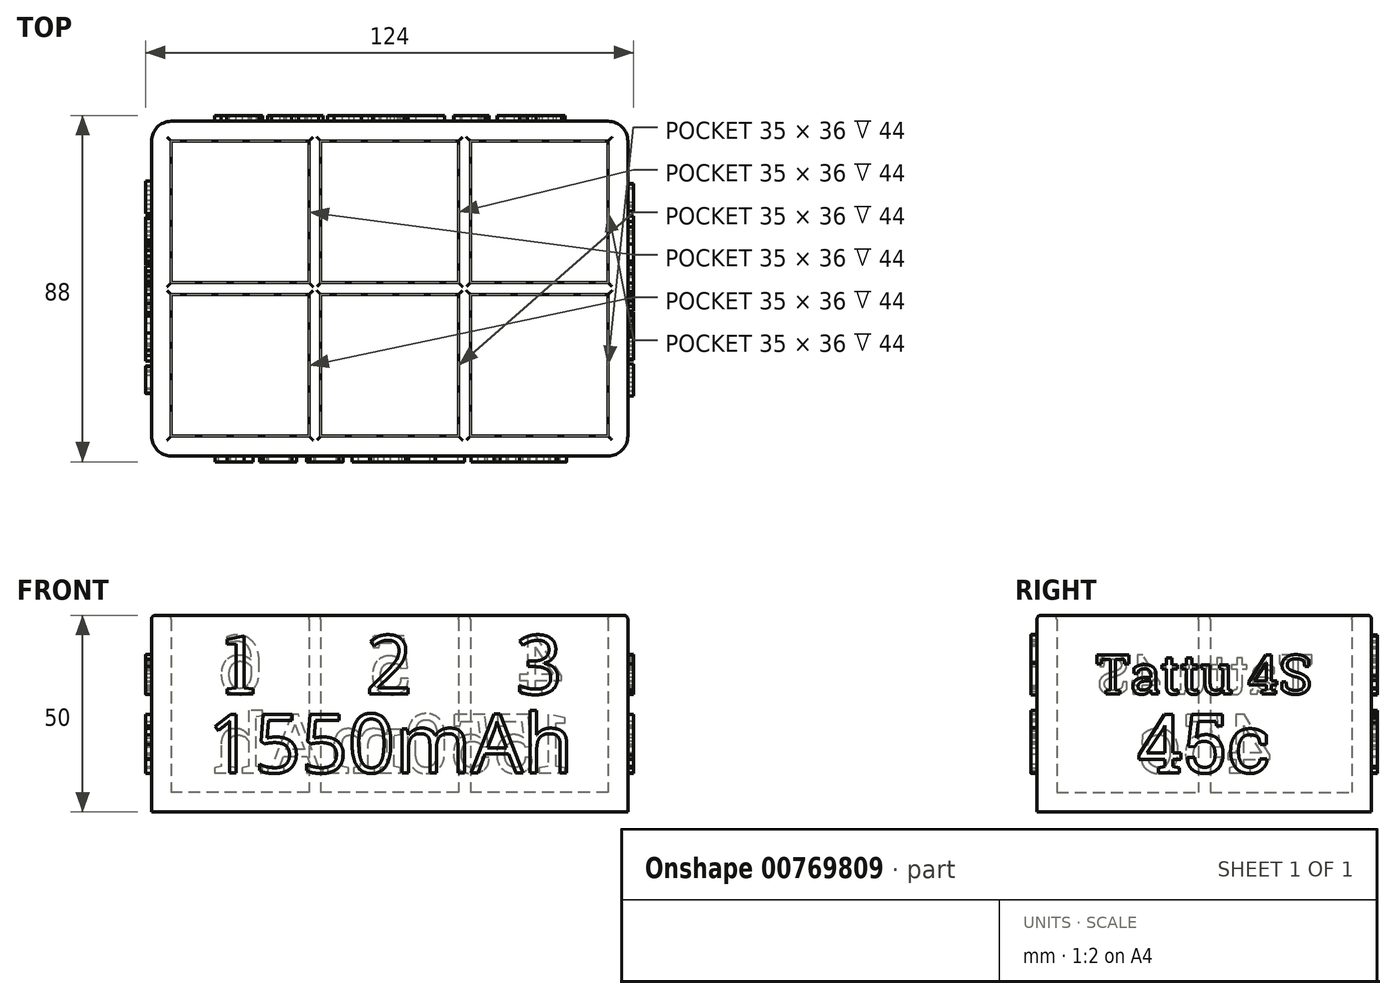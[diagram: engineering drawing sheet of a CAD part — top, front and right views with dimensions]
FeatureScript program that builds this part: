
annotation { "Feature Type Name" : "Feature", "Feature Type Description" : "" }
export const myFeature = defineFeature(function(context is Context, id is Id, definition is map)
    precondition{}
    {
        {
            var Q0;
            Q0=qCreatedBy(makeId("Top.planeOp"),FACE);
            var sketch = newSketch(context, id + "F0", { "sketchPlane" : qUnion([Q0])});
            skLineSegment(sketch, "E0.bottom", {"start": v(17.5, -18) * mm, "end": v(-17.5, -18) * mm});
            skLineSegment(sketch, "E0.top", {"start": v(17.5, 18) * mm, "end": v(-17.5, 18) * mm});
            skLineSegment(sketch, "E0.left", {"start": v(17.5, -18) * mm, "end": v(17.5, 18) * mm});
            skLineSegment(sketch, "E0.right", {"start": v(-17.5, -18) * mm, "end": v(-17.5, 18) * mm});
            skPoint(sketch, "E0.middle", {"position": v(0, 0) * mm});
            skLineSegment(sketch, "E1.0.1.0", {"start": v(17.5, 57) * mm, "end": v(-17.5, 57) * mm});
            skLineSegment(sketch, "E1.0.1.1", {"start": v(-17.5, 21) * mm, "end": v(-17.5, 57) * mm});
            skLineSegment(sketch, "E1.0.1.2", {"start": v(17.5, 21) * mm, "end": v(-17.5, 21) * mm});
            skLineSegment(sketch, "E1.0.1.3", {"start": v(17.5, 21) * mm, "end": v(17.5, 57) * mm});
            skLineSegment(sketch, "E1.1.0.0", {"start": v(55.5, 18) * mm, "end": v(20.5, 18) * mm});
            skLineSegment(sketch, "E1.1.0.1", {"start": v(20.5, -18) * mm, "end": v(20.5, 18) * mm});
            skLineSegment(sketch, "E1.1.0.2", {"start": v(55.5, -18) * mm, "end": v(20.5, -18) * mm});
            skLineSegment(sketch, "E1.1.0.3", {"start": v(55.5, -18) * mm, "end": v(55.5, 18) * mm});
            skLineSegment(sketch, "E1.1.1.0", {"start": v(55.5, 57) * mm, "end": v(20.5, 57) * mm});
            skLineSegment(sketch, "E1.1.1.1", {"start": v(20.5, 21) * mm, "end": v(20.5, 57) * mm});
            skLineSegment(sketch, "E1.1.1.2", {"start": v(55.5, 21) * mm, "end": v(20.5, 21) * mm});
            skLineSegment(sketch, "E1.1.1.3", {"start": v(55.5, 21) * mm, "end": v(55.5, 57) * mm});
            skLineSegment(sketch, "E1.2.0.0", {"start": v(93.5, 18) * mm, "end": v(58.5, 18) * mm});
            skLineSegment(sketch, "E1.2.0.1", {"start": v(58.5, -18) * mm, "end": v(58.5, 18) * mm});
            skLineSegment(sketch, "E1.2.0.2", {"start": v(93.5, -18) * mm, "end": v(58.5, -18) * mm});
            skLineSegment(sketch, "E1.2.0.3", {"start": v(93.5, -18) * mm, "end": v(93.5, 18) * mm});
            skLineSegment(sketch, "E1.2.1.0", {"start": v(93.5, 57) * mm, "end": v(58.5, 57) * mm});
            skLineSegment(sketch, "E1.2.1.1", {"start": v(58.5, 21) * mm, "end": v(58.5, 57) * mm});
            skLineSegment(sketch, "E1.2.1.2", {"start": v(93.5, 21) * mm, "end": v(58.5, 21) * mm});
            skLineSegment(sketch, "E1.2.1.3", {"start": v(93.5, 21) * mm, "end": v(93.5, 57) * mm});
            skLineSegment(sketch, "E1.direction1", {"start": v(-17.5, 18) * mm, "end": v(20.5, 18) * mm, "construction": true});
            skLineSegment(sketch, "E1.direction2", {"start": v(-17.5, 18) * mm, "end": v(-17.5, 57) * mm, "construction": true});
            skLineSegment(sketch, "E2.bottom", {"start": v(-22.5, 62) * mm, "end": v(98.5, 62) * mm});
            skLineSegment(sketch, "E2.top", {"start": v(-22.5, -23) * mm, "end": v(98.5, -23) * mm});
            skLineSegment(sketch, "E2.left", {"start": v(-22.5, 62) * mm, "end": v(-22.5, -23) * mm});
            skLineSegment(sketch, "E2.right", {"start": v(98.5, 62) * mm, "end": v(98.5, -23) * mm});
            skSolve(sketch);
        }
        {
            var Q0;
            Q0=makeQuery(id+"F0.imprint","IMPRINT",FACE,{"disambiguationData":[TD([[makeQuery(id+"F0.imprint","IMPRINT",EDGE,{"derivedFrom":sQuery(id+"F0.wireOp",EDGE,"E0.bottom")}),1.0]])]});
            var Q1;
            Q1=makeQuery(id+"F0.imprint","IMPRINT",FACE,{"disambiguationData":[TD([[makeQuery(id+"F0.imprint","IMPRINT",EDGE,{"derivedFrom":sQuery(id+"F0.wireOp",EDGE,"E0.bottom")}),-1.0]])]});
            var Q2;
            Q2=makeQuery(id+"F0.imprint","IMPRINT",FACE,{"disambiguationData":[TD([[makeQuery(id+"F0.imprint","IMPRINT",EDGE,{"derivedFrom":sQuery(id+"F0.wireOp",EDGE,"E1.0.1.0")}),1.0]])]});
            var Q3;
            Q3=makeQuery(id+"F0.imprint","IMPRINT",FACE,{"disambiguationData":[TD([[makeQuery(id+"F0.imprint","IMPRINT",EDGE,{"derivedFrom":sQuery(id+"F0.wireOp",EDGE,"E1.1.0.0")}),1.0]])]});
            var Q4;
            Q4=makeQuery(id+"F0.imprint","IMPRINT",FACE,{"disambiguationData":[TD([[makeQuery(id+"F0.imprint","IMPRINT",EDGE,{"derivedFrom":sQuery(id+"F0.wireOp",EDGE,"E1.1.1.0")}),1.0]])]});
            var Q5;
            Q5=makeQuery(id+"F0.imprint","IMPRINT",FACE,{"disambiguationData":[TD([[makeQuery(id+"F0.imprint","IMPRINT",EDGE,{"derivedFrom":sQuery(id+"F0.wireOp",EDGE,"E1.2.1.0")}),1.0]])]});
            var Q6;
            Q6=makeQuery(id+"F0.imprint","IMPRINT",FACE,{"disambiguationData":[TD([[makeQuery(id+"F0.imprint","IMPRINT",EDGE,{"derivedFrom":sQuery(id+"F0.wireOp",EDGE,"E1.2.0.0")}),1.0]])]});
            extrude(context, id + "F1", {"entities" : qUnion([Q0, Q1, Q2, Q3, Q4, Q5, Q6]), "oppositeDirection" : true, "depth" : 5 * mm, "offsetDistance" : 25 * mm});
        }
        {
            var Q0;
            Q0=makeQuery(id+"F0.imprint","IMPRINT",FACE,{"disambiguationData":[TD([[makeQuery(id+"F0.imprint","IMPRINT",EDGE,{"derivedFrom":sQuery(id+"F0.wireOp",EDGE,"E0.bottom")}),1.0]])]});
            extrude(context, id + "F2", {"entities" : qUnion([Q0]), "operationType" : NewBodyOperationType.ADD, "depth" : 45 * mm, "offsetDistance" : 25 * mm});
        }
        {
            var Q0;
            {var subQ0=sQuery(id+"F0.wireOp",EDGE,"E2.top");Q0=makeQuery(id+"F2.boolean.opBoolean","MERGE",FACE,{"derivedFrom":[makeQuery(id+"F1.opExtrude","SWEPT_FACE",FACE,{"disambiguationData":[OSD([subQ0])]}),makeQuery(id+"F2.opExtrude","SWEPT_FACE",FACE,{"disambiguationData":[OSD([subQ0])]})]});}
            var sketch = newSketch(context, id + "F3", { "sketchPlane" : qUnion([Q0])});
            skLineSegment(sketch, "E3", {"start": v(-59.84, 40) * mm, "end": v(123.55, 40) * mm, "construction": true});
            skLineSegment(sketch, "E4", {"start": v(-60.92, 25) * mm, "end": v(136.92, 25) * mm, "construction": true});
            skLineSegment(sketch, "E5", {"start": v(0, 84.5) * mm, "end": v(0, -27.53) * mm, "construction": true});
            skLineSegment(sketch, "E6", {"start": v(38, 84.3) * mm, "end": v(38, -24.79) * mm, "construction": true});
            skLineSegment(sketch, "E7", {"start": v(76, 82.1) * mm, "end": v(76, -27.2) * mm, "construction": true});
            skText(sketch, "E8", { "text": "1", "fontName": "RobotoSlab-Regular.ttf"});
            skText(sketch, "E9", { "text": "2", "fontName": "OpenSans-Regular.ttf"});
            skText(sketch, "E10", { "text": "3", "fontName": "OpenSans-Regular.ttf"});
            skText(sketch, "E11", { "text": "1550mAh", "fontName": "OpenSans-Regular.ttf"});
            const initialGuessF3  = {"E8": [-0.00455, 0.025, 1, 0, 0.015], "E9": [0.03193, 0.025, 1, 0, 0.015], "E10": [0.06998, 0.025, 1, 0, 0.015], "E11": [-0.00833, 0.005, 1, 0, 0.015]};
            skSetInitialGuess(sketch, initialGuessF3);
            skSolve(sketch);
        }
        {
            var Q0;
            {var subQ0=sQuery(id+"F0.wireOp",EDGE,"E2.bottom");Q0=makeQuery(id+"F2.boolean.opBoolean","MERGE",FACE,{"derivedFrom":[makeQuery(id+"F1.opExtrude","SWEPT_FACE",FACE,{"disambiguationData":[OSD([subQ0])]}),makeQuery(id+"F2.opExtrude","SWEPT_FACE",FACE,{"disambiguationData":[OSD([subQ0])]})]});}
            var sketch = newSketch(context, id + "F4", { "sketchPlane" : qUnion([Q0])});
            skLineSegment(sketch, "E12", {"start": v(-177.3, 40) * mm, "end": v(6.09, 40) * mm, "construction": true});
            skLineSegment(sketch, "E13", {"start": v(-178.38, 25) * mm, "end": v(19.46, 25) * mm, "construction": true});
            skLineSegment(sketch, "E14", {"start": v(-76, 83.96) * mm, "end": v(-76, -28.07) * mm, "construction": true});
            skLineSegment(sketch, "E15", {"start": v(-38, 83.76) * mm, "end": v(-38, -25.32) * mm, "construction": true});
            skLineSegment(sketch, "E16", {"start": v(0, 81.57) * mm, "end": v(0, -27.73) * mm, "construction": true});
            skText(sketch, "E17", { "text": "4", "fontName": "RobotoSlab-Regular.ttf"});
            skText(sketch, "E18", { "text": "5", "fontName": "RobotoSlab-Regular.ttf"});
            skText(sketch, "E19", { "text": "6", "fontName": "RobotoSlab-Regular.ttf"});
            skText(sketch, "E20", { "text": "1550mAh", "fontName": "RobotoSlab-Regular.ttf"});
            const initialGuessF4  = {"E17": [-0.08231, 0.025, 1, 0, 0.015], "E18": [-0.04364, 0.025, 1, 0, 0.015], "E19": [-0.00607, 0.025, 1, 0, 0.015], "E20": [-0.0838, 0.005, 1, 0, 0.015]};
            skSetInitialGuess(sketch, initialGuessF4);
            skSolve(sketch);
        }
        {
            var Q0;
            Q0 = qSketchRegion(id + "F4", true);
            extrude(context, id + "F5", {"entities" : qUnion([Q0]), "operationType" : NewBodyOperationType.ADD, "depth" : 1.5 * mm, "offsetDistance" : 25 * mm});
        }
        {
            var Q0;
            Q0 = qSketchRegion(id + "F3", true);
            extrude(context, id + "F6", {"entities" : qUnion([Q0]), "operationType" : NewBodyOperationType.ADD, "depth" : 1.5 * mm, "offsetDistance" : 25 * mm});
        }
        {
            var Q0;
            {var subQ0=sQuery(id+"F0.wireOp",EDGE,"E2.left");Q0=makeQuery(id+"F2.boolean.opBoolean","MERGE",FACE,{"derivedFrom":[makeQuery(id+"F1.opExtrude","SWEPT_FACE",FACE,{"disambiguationData":[OSD([subQ0])]}),makeQuery(id+"F2.opExtrude","SWEPT_FACE",FACE,{"disambiguationData":[OSD([subQ0])]})]});}
            var sketch = newSketch(context, id + "F7", { "sketchPlane" : qUnion([Q0])});
            skText(sketch, "E21", { "text": "Tattu 4S", "fontName": "RobotoSlab-Regular.ttf"});
            skLineSegment(sketch, "E22", {"start": v(-19.5, 84.5) * mm, "end": v(-19.5, -25.36) * mm, "construction": true});
            skLineSegment(sketch, "E23", {"start": v(49.66, 35) * mm, "end": v(-83.48, 35) * mm, "construction": true});
            skLineSegment(sketch, "E24", {"start": v(-87.5, 25) * mm, "end": v(51.92, 25) * mm, "construction": true});
            skText(sketch, "E25", { "text": "45c", "fontName": "RobotoSlab-Regular.ttf"});
            const initialGuessF7  = {"E21": [-0.04707, 0.025, 1, 0, 0.01], "E25": [-0.0368, 0.005, 1, 0, 0.015]};
            skSetInitialGuess(sketch, initialGuessF7);
            skSolve(sketch);
        }
        {
            var Q0;
            {var subQ0=sQuery(id+"F0.wireOp",EDGE,"E2.right");Q0=makeQuery(id+"F2.boolean.opBoolean","MERGE",FACE,{"derivedFrom":[makeQuery(id+"F1.opExtrude","SWEPT_FACE",FACE,{"disambiguationData":[OSD([subQ0])]}),makeQuery(id+"F2.opExtrude","SWEPT_FACE",FACE,{"disambiguationData":[OSD([subQ0])]})]});}
            var sketch = newSketch(context, id + "F8", { "sketchPlane" : qUnion([Q0])});
            skText(sketch, "E26", { "text": "Tattu 4S", "fontName": "RobotoSlab-Regular.ttf"});
            skLineSegment(sketch, "E27", {"start": v(19.5, 94.6) * mm, "end": v(19.5, -15.27) * mm, "construction": true});
            skLineSegment(sketch, "E28", {"start": v(88.66, 35) * mm, "end": v(-44.48, 35) * mm, "construction": true});
            skLineSegment(sketch, "E29", {"start": v(-48.5, 25) * mm, "end": v(90.92, 25) * mm, "construction": true});
            skText(sketch, "E30", { "text": "45c", "fontName": "RobotoSlab-Regular.ttf"});
            const initialGuessF8  = {"E26": [-0.00807, 0.025, 1, 0, 0.01], "E30": [0.0022, 0.005, 1, 0, 0.015]};
            skSetInitialGuess(sketch, initialGuessF8);
            skSolve(sketch);
        }
        {
            var Q0;
            Q0 = qSketchRegion(id + "F8", true);
            extrude(context, id + "F9", {"entities" : qUnion([Q0]), "operationType" : NewBodyOperationType.ADD, "depth" : 1.5 * mm, "offsetDistance" : 25 * mm});
        }
        {
            var Q0;
            Q0 = qSketchRegion(id + "F7", true);
            extrude(context, id + "F10", {"entities" : qUnion([Q0]), "operationType" : NewBodyOperationType.ADD, "depth" : 1.5 * mm, "offsetDistance" : 25 * mm});
        }
        {
            var Q0;
            {var subQ0=sQuery(id+"F0.wireOp",EDGE,"E2.left");var subQ1=sQuery(id+"F0.wireOp",EDGE,"E2.top");Q0=makeQuery(id+"F2.boolean.opBoolean","MERGE",EDGE,{"derivedFrom":[makeQuery(id+"F1.opExtrude","SWEPT_EDGE",EDGE,{"disambiguationData":[OSD([subQ1,subQ0])]}),makeQuery(id+"F2.opExtrude","SWEPT_EDGE",EDGE,{"disambiguationData":[OSD([subQ1,subQ0])]})]});}
            var Q1;
            {var subQ0=sQuery(id+"F0.wireOp",EDGE,"E2.right");var subQ1=sQuery(id+"F0.wireOp",EDGE,"E2.top");Q1=makeQuery(id+"F2.boolean.opBoolean","MERGE",EDGE,{"derivedFrom":[makeQuery(id+"F1.opExtrude","SWEPT_EDGE",EDGE,{"disambiguationData":[OSD([subQ1,subQ0])]}),makeQuery(id+"F2.opExtrude","SWEPT_EDGE",EDGE,{"disambiguationData":[OSD([subQ1,subQ0])]})]});}
            var Q2;
            {var subQ0=sQuery(id+"F0.wireOp",EDGE,"E2.right");var subQ1=sQuery(id+"F0.wireOp",EDGE,"E2.bottom");Q2=makeQuery(id+"F2.boolean.opBoolean","MERGE",EDGE,{"derivedFrom":[makeQuery(id+"F1.opExtrude","SWEPT_EDGE",EDGE,{"disambiguationData":[OSD([subQ1,subQ0])]}),makeQuery(id+"F2.opExtrude","SWEPT_EDGE",EDGE,{"disambiguationData":[OSD([subQ1,subQ0])]})]});}
            var Q3;
            {var subQ0=sQuery(id+"F0.wireOp",EDGE,"E2.left");var subQ1=sQuery(id+"F0.wireOp",EDGE,"E2.bottom");Q3=makeQuery(id+"F2.boolean.opBoolean","MERGE",EDGE,{"derivedFrom":[makeQuery(id+"F1.opExtrude","SWEPT_EDGE",EDGE,{"disambiguationData":[OSD([subQ1,subQ0])]}),makeQuery(id+"F2.opExtrude","SWEPT_EDGE",EDGE,{"disambiguationData":[OSD([subQ1,subQ0])]})]});}
            fillet(context, id + "F11", {"entities" : qUnion([Q0, Q1, Q2, Q3]), "radius" : 5 * mm, "tangentPropagation" : true, "allowEdgeOverflow" : false});
        }
        {
            var Q0;
            Q0=makeQuery(id+"F2.opExtrude","CAP_EDGE",EDGE,{"disambiguationData":[OSD([sQuery(id+"F0.wireOp",EDGE,"E1.2.0.2")])],"isStart":false});
            var Q1;
            Q1=makeQuery(id+"F2.opExtrude","CAP_EDGE",EDGE,{"disambiguationData":[OSD([sQuery(id+"F0.wireOp",EDGE,"E1.2.0.1")])],"isStart":false});
            var Q2;
            Q2=makeQuery(id+"F2.opExtrude","CAP_EDGE",EDGE,{"disambiguationData":[OSD([sQuery(id+"F0.wireOp",EDGE,"E1.2.0.0")])],"isStart":false});
            var Q3;
            Q3=makeQuery(id+"F2.opExtrude","CAP_EDGE",EDGE,{"disambiguationData":[OSD([sQuery(id+"F0.wireOp",EDGE,"E1.2.0.3")])],"isStart":false});
            var Q4;
            Q4=makeQuery(id+"F2.opExtrude","CAP_EDGE",EDGE,{"disambiguationData":[OSD([sQuery(id+"F0.wireOp",EDGE,"E1.1.0.2")])],"isStart":false});
            var Q5;
            Q5=makeQuery(id+"F2.opExtrude","CAP_EDGE",EDGE,{"disambiguationData":[OSD([sQuery(id+"F0.wireOp",EDGE,"E0.bottom")])],"isStart":false});
            var Q6;
            Q6=makeQuery(id+"F2.opExtrude","CAP_EDGE",EDGE,{"disambiguationData":[OSD([sQuery(id+"F0.wireOp",EDGE,"E0.left")])],"isStart":false});
            var Q7;
            Q7=makeQuery(id+"F2.opExtrude","CAP_EDGE",EDGE,{"disambiguationData":[OSD([sQuery(id+"F0.wireOp",EDGE,"E1.1.0.1")])],"isStart":false});
            var Q8;
            Q8=makeQuery(id+"F2.opExtrude","CAP_EDGE",EDGE,{"disambiguationData":[OSD([sQuery(id+"F0.wireOp",EDGE,"E1.1.0.3")])],"isStart":false});
            var Q9;
            Q9=makeQuery(id+"F2.opExtrude","CAP_EDGE",EDGE,{"disambiguationData":[OSD([sQuery(id+"F0.wireOp",EDGE,"E0.right")])],"isStart":false});
            var Q10;
            Q10=makeQuery(id+"F2.opExtrude","CAP_EDGE",EDGE,{"disambiguationData":[OSD([sQuery(id+"F0.wireOp",EDGE,"E0.top")])],"isStart":false});
            var Q11;
            Q11=makeQuery(id+"F2.opExtrude","CAP_EDGE",EDGE,{"disambiguationData":[OSD([sQuery(id+"F0.wireOp",EDGE,"E1.0.1.2")])],"isStart":false});
            var Q12;
            Q12=makeQuery(id+"F2.opExtrude","CAP_EDGE",EDGE,{"disambiguationData":[OSD([sQuery(id+"F0.wireOp",EDGE,"E1.1.0.0")])],"isStart":false});
            var Q13;
            Q13=makeQuery(id+"F2.opExtrude","CAP_EDGE",EDGE,{"disambiguationData":[OSD([sQuery(id+"F0.wireOp",EDGE,"E1.1.1.2")])],"isStart":false});
            var Q14;
            Q14=makeQuery(id+"F2.opExtrude","CAP_EDGE",EDGE,{"disambiguationData":[OSD([sQuery(id+"F0.wireOp",EDGE,"E1.2.1.2")])],"isStart":false});
            var Q15;
            Q15=makeQuery(id+"F2.opExtrude","CAP_EDGE",EDGE,{"disambiguationData":[OSD([sQuery(id+"F0.wireOp",EDGE,"E1.2.1.1")])],"isStart":false});
            var Q16;
            Q16=makeQuery(id+"F2.opExtrude","CAP_EDGE",EDGE,{"disambiguationData":[OSD([sQuery(id+"F0.wireOp",EDGE,"E1.2.1.0")])],"isStart":false});
            var Q17;
            Q17=makeQuery(id+"F2.opExtrude","CAP_EDGE",EDGE,{"disambiguationData":[OSD([sQuery(id+"F0.wireOp",EDGE,"E1.2.1.3")])],"isStart":false});
            var Q18;
            Q18=makeQuery(id+"F2.opExtrude","CAP_EDGE",EDGE,{"disambiguationData":[OSD([sQuery(id+"F0.wireOp",EDGE,"E1.1.1.3")])],"isStart":false});
            var Q19;
            Q19=makeQuery(id+"F2.opExtrude","CAP_EDGE",EDGE,{"disambiguationData":[OSD([sQuery(id+"F0.wireOp",EDGE,"E1.1.1.0")])],"isStart":false});
            var Q20;
            Q20=makeQuery(id+"F2.opExtrude","CAP_EDGE",EDGE,{"disambiguationData":[OSD([sQuery(id+"F0.wireOp",EDGE,"E1.1.1.1")])],"isStart":false});
            var Q21;
            Q21=makeQuery(id+"F2.opExtrude","CAP_EDGE",EDGE,{"disambiguationData":[OSD([sQuery(id+"F0.wireOp",EDGE,"E1.0.1.3")])],"isStart":false});
            var Q22;
            Q22=makeQuery(id+"F2.opExtrude","CAP_EDGE",EDGE,{"disambiguationData":[OSD([sQuery(id+"F0.wireOp",EDGE,"E1.0.1.0")])],"isStart":false});
            var Q23;
            Q23=makeQuery(id+"F2.opExtrude","CAP_EDGE",EDGE,{"disambiguationData":[OSD([sQuery(id+"F0.wireOp",EDGE,"E1.0.1.1")])],"isStart":false});
            var Q24;
            Q24=makeQuery(id+"F2.opExtrude","CAP_EDGE",EDGE,{"disambiguationData":[OSD([sQuery(id+"F0.wireOp",EDGE,"E2.top")])],"isStart":false});
            var Q25;
            Q25=makeQuery(id+"F2.opExtrude","CAP_EDGE",EDGE,{"disambiguationData":[OSD([sQuery(id+"F0.wireOp",EDGE,"E2.right")])],"isStart":false});
            fillet(context, id + "F12", {"entities" : qUnion([Q0, Q1, Q2, Q3, Q4, Q5, Q6, Q7, Q8, Q9, Q10, Q11, Q12, Q13, Q14, Q15, Q16, Q17, Q18, Q19, Q20, Q21, Q22, Q23, Q24, Q25]), "radius" : 1 * mm, "tangentPropagation" : true, "allowEdgeOverflow" : false});
        }
    });
